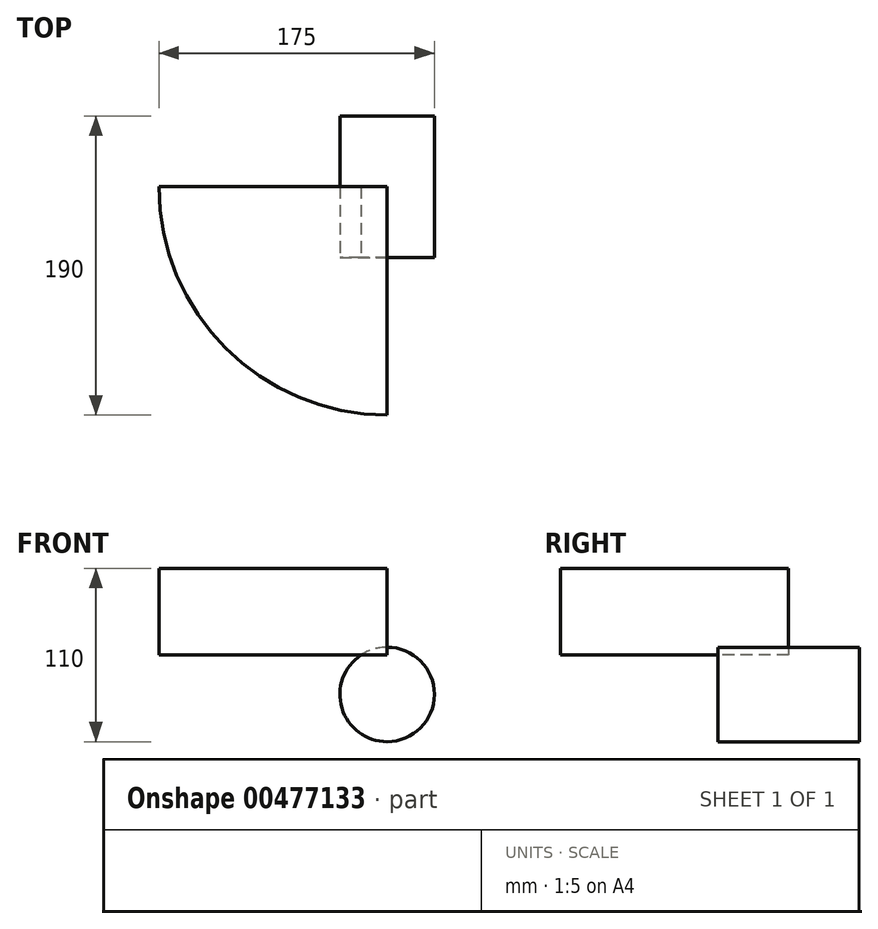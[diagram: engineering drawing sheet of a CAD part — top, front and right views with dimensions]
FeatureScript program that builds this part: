
annotation { "Feature Type Name" : "Feature", "Feature Type Description" : "" }
export const myFeature = defineFeature(function(context is Context, id is Id, definition is map)
    precondition{}
    {
        {
            var Q0;
            Q0=qCreatedBy(makeId("Front.planeOp"),FACE);
            var sketch = newSketch(context, id + "F0", { "sketchPlane" : qUnion([Q0])});
            skCircle(sketch, "E0", {"center": v(0, -30) * mm, "radius": 30 * mm});
            skSolve(sketch);
        }
        {
            var Q0;
            Q0 = qSketchRegion(id + "F0", true);
            extrude(context, id + "F1", {"entities" : qUnion([Q0]), "oppositeDirection" : true, "depth" : 90 * mm, "offsetDistance" : 25 * mm});
        }
        {
            var Q0;
            Q0=qCreatedBy(makeId("Top.planeOp"),FACE);
            var sketch = newSketch(context, id + "F2", { "sketchPlane" : qUnion([Q0])});
            skLineSegment(sketch, "E1", {"start": v(-30, 0) * mm, "end": v(-30, 90) * mm, "construction": true});
            skLineSegment(sketch, "E2", {"start": v(30, 90) * mm, "end": v(30, 0) * mm, "construction": true});
            skLineSegment(sketch, "E3", {"start": v(-30, 45) * mm, "end": v(30, 45) * mm, "construction": true});
            skLineSegment(sketch, "E4.0", {"start": v(30, 90) * mm, "end": v(-30, 90) * mm, "construction": true});
            skLineSegment(sketch, "E5.0", {"start": v(30, 0) * mm, "end": v(-30, 0) * mm, "construction": true});
            skLineSegment(sketch, "E6", {"start": v(0, 90) * mm, "end": v(0, 0) * mm, "construction": true});
            skLineSegment(sketch, "E7", {"start": v(0, 45) * mm, "end": v(-145, 45) * mm});
            skLineSegment(sketch, "E8", {"start": v(0, 45) * mm, "end": v(0, -100) * mm});
            skArc(sketch, "E9", {"start": v(0, -100) * mm, "mid": v(-102.53, -57.53) * mm, "end": v(-145, 45) * mm});
            skSolve(sketch);
        }
        {
            var Q0;
            Q0=makeQuery(id+"F2.imprint","IMPRINT",FACE,{"disambiguationData":[TD([[makeQuery(id+"F2.imprint","IMPRINT",EDGE,{"derivedFrom":sQuery(id+"F2.wireOp",EDGE,"E7")}),1.0]])]});
            extrude(context, id + "F3", {"entities" : qUnion([Q0]), "operationType" : NewBodyOperationType.ADD, "depth" : 50 * mm, "offsetDistance" : 25 * mm, "hasSecondDirection" : true, "secondDirectionOppositeDirection" : true, "secondDirectionDepth" : 5 * mm});
        }
    });
